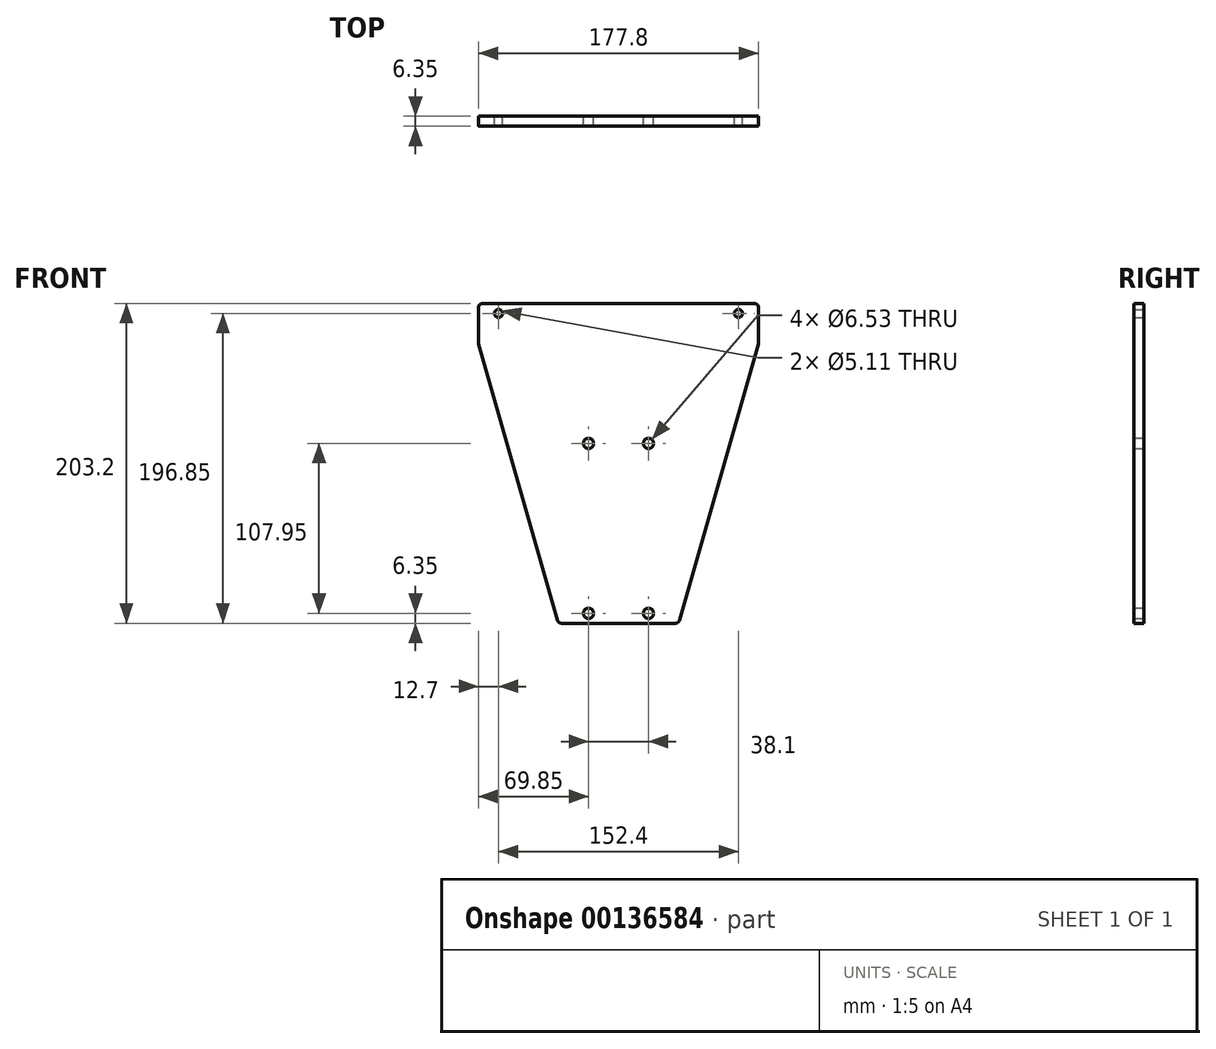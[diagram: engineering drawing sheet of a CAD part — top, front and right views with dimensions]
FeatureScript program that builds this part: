
annotation { "Feature Type Name" : "Feature", "Feature Type Description" : "" }
export const myFeature = defineFeature(function(context is Context, id is Id, definition is map)
    precondition{}
    {
        {
            var Q0;
            Q0=qCreatedBy(makeId("Front.planeOp"),FACE);
            var sketch = newSketch(context, id + "F0", { "sketchPlane" : qUnion([Q0])});
            skLineSegment(sketch, "E0.bottom", {"start": v(2.54, 0) * mm, "end": v(175.26, 0) * mm});
            skLineSegment(sketch, "E0.top", {"start": v(52.72, -203.2) * mm, "end": v(125.08, -203.2) * mm});
            skLineSegment(sketch, "E0.left", {"start": v(0, -25.04) * mm, "end": v(0, -2.54) * mm});
            skLineSegment(sketch, "E0.right", {"start": v(177.8, -25.04) * mm, "end": v(177.8, -2.54) * mm});
            skLineSegment(sketch, "E1", {"start": v(88.9, -203.2) * mm, "end": v(88.9, 0) * mm, "construction": true});
            skCircle(sketch, "E2", {"center": v(69.85, -196.85) * mm, "radius": 3.26 * mm});
            skCircle(sketch, "E3.0.1.0", {"center": v(69.85, -88.9) * mm, "radius": 3.26 * mm});
            skCircle(sketch, "E3.1.0.0", {"center": v(107.95, -196.85) * mm, "radius": 3.26 * mm});
            skCircle(sketch, "E3.1.1.0", {"center": v(107.95, -88.9) * mm, "radius": 3.26 * mm});
            skLineSegment(sketch, "E3.direction1", {"start": v(69.85, -196.85) * mm, "end": v(107.95, -196.85) * mm, "construction": true});
            skLineSegment(sketch, "E3.direction2", {"start": v(69.85, -196.85) * mm, "end": v(69.85, -88.9) * mm, "construction": true});
            skCircle(sketch, "E4", {"center": v(12.7, -6.35) * mm, "radius": 2.55 * mm});
            skCircle(sketch, "E5", {"center": v(165.1, -6.35) * mm, "radius": 2.55 * mm});
            skLineSegment(sketch, "E6", {"start": v(12.7, -6.35) * mm, "end": v(165.1, -6.35) * mm, "construction": true});
            skLineSegment(sketch, "E7", {"start": v(0.1, -25.74) * mm, "end": v(50.27, -201.36) * mm});
            skLineSegment(sketch, "E8.MirrorCS", {"start": v(177.7, -25.74) * mm, "end": v(127.53, -201.36) * mm});
            skPoint(sketch, "E9.orphan", {"position": v(177.8, -203.2) * mm});
            skPoint(sketch, "E10.orphan", {"position": v(0, -203.2) * mm});
            skCircle(sketch, "E11", {"center": v(12.7, -6.35) * mm, "radius": 152.4 * mm, "construction": true});
            skLineSegment(sketch, "E12", {"start": v(12.7, -6.35) * mm, "end": v(36.25, -78.82) * mm, "construction": true});
            skPoint(sketch, "E13", {"position": v(132.87, -47.42) * mm});
            skLineSegment(sketch, "E14", {"start": v(36.25, -78.82) * mm, "end": v(132.87, -47.42) * mm, "construction": true});
            skLineSegment(sketch, "E15", {"start": v(132.87, -47.42) * mm, "end": v(169.1, -35.65) * mm});
            skLineSegment(sketch, "E16.1.0", {"start": v(133.57, -45.32) * mm, "end": v(169.6, -32.92) * mm});
            skLineSegment(sketch, "E16.2.0", {"start": v(134.23, -43.2) * mm, "end": v(170.04, -30.17) * mm});
            skLineSegment(sketch, "E16.3.0", {"start": v(134.86, -41.08) * mm, "end": v(170.43, -27.42) * mm});
            skLineSegment(sketch, "E16.4.0", {"start": v(135.45, -38.94) * mm, "end": v(170.77, -24.67) * mm});
            skLineSegment(sketch, "E16.5.0", {"start": v(136, -36.8) * mm, "end": v(171.07, -21.9) * mm});
            skLineSegment(sketch, "E16.6.0", {"start": v(136.5, -34.64) * mm, "end": v(171.32, -19.14) * mm});
            skLineSegment(sketch, "E16.7.0", {"start": v(136.98, -32.47) * mm, "end": v(171.51, -16.37) * mm});
            skLineSegment(sketch, "E16.8.0", {"start": v(137.42, -30.3) * mm, "end": v(171.67, -13.6) * mm});
            skLineSegment(sketch, "E16.anchor1", {"start": v(12.7, -6.35) * mm, "end": v(132.87, -47.42) * mm, "construction": true});
            skLineSegment(sketch, "E16.anchor2", {"start": v(12.7, -6.35) * mm, "end": v(137.42, -30.3) * mm, "construction": true});
            skLineSegment(sketch, "E17.1.0", {"start": v(132.14, -49.52) * mm, "end": v(168.57, -38.38) * mm});
            skLineSegment(sketch, "E17.2.0", {"start": v(131.37, -51.6) * mm, "end": v(168, -41.1) * mm});
            skLineSegment(sketch, "E17.3.0", {"start": v(130.56, -53.66) * mm, "end": v(167.36, -43.8) * mm});
            skLineSegment(sketch, "E17.4.0", {"start": v(129.72, -55.7) * mm, "end": v(166.68, -46.5) * mm});
            skLineSegment(sketch, "E17.5.0", {"start": v(128.84, -57.74) * mm, "end": v(165.96, -49.17) * mm});
            skLineSegment(sketch, "E17.6.0", {"start": v(127.92, -59.76) * mm, "end": v(165.2, -51.84) * mm});
            skLineSegment(sketch, "E17.7.0", {"start": v(126.97, -61.76) * mm, "end": v(164.37, -54.5) * mm});
            skLineSegment(sketch, "E17.8.0", {"start": v(125.99, -63.75) * mm, "end": v(163.5, -57.13) * mm});
            skLineSegment(sketch, "E17.anchor2", {"start": v(12.7, -6.35) * mm, "end": v(125.99, -63.75) * mm, "construction": true});
            skPoint(sketch, "E18.visualSharp", {"position": v(0, 0) * mm});
            skArc(sketch, "E18.filletArc", {"start": v(2.54, 0) * mm, "mid": v(0.74, -0.74) * mm, "end": v(0, -2.54) * mm});
            skPoint(sketch, "E19.visualSharp", {"position": v(177.8, 0) * mm});
            skArc(sketch, "E19.filletArc", {"start": v(177.8, -2.54) * mm, "mid": v(177.06, -0.74) * mm, "end": v(175.26, 0) * mm});
            skPoint(sketch, "E20.visualSharp", {"position": v(177.8, -25.4) * mm});
            skArc(sketch, "E20.filletArc", {"start": v(177.7, -25.74) * mm, "mid": v(177.78, -25.4) * mm, "end": v(177.8, -25.04) * mm});
            skPoint(sketch, "E21.visualSharp", {"position": v(0, -25.4) * mm});
            skArc(sketch, "E21.filletArc", {"start": v(0, -25.04) * mm, "mid": v(0.02, -25.4) * mm, "end": v(0.1, -25.74) * mm});
            skPoint(sketch, "E22.visualSharp", {"position": v(127, -203.2) * mm});
            skArc(sketch, "E22.filletArc", {"start": v(125.08, -203.2) * mm, "mid": v(126.61, -202.69) * mm, "end": v(127.53, -201.36) * mm});
            skPoint(sketch, "E23.visualSharp", {"position": v(50.8, -203.2) * mm});
            skArc(sketch, "E23.filletArc", {"start": v(50.27, -201.36) * mm, "mid": v(51.19, -202.69) * mm, "end": v(52.72, -203.2) * mm});
            skSolve(sketch);
        }
        {
            var Q0;
            Q0=makeQuery(id+"F0.imprint","IMPRINT",FACE,{"disambiguationData":[TD([[makeQuery(id+"F0.imprint","IMPRINT",EDGE,{"derivedFrom":sQuery(id+"F0.wireOp",EDGE,"E0.bottom")}),-1.0]])]});
            extrude(context, id + "F1", {"entities" : qUnion([Q0]), "depth" : 6.35 * mm});
        }
    });
